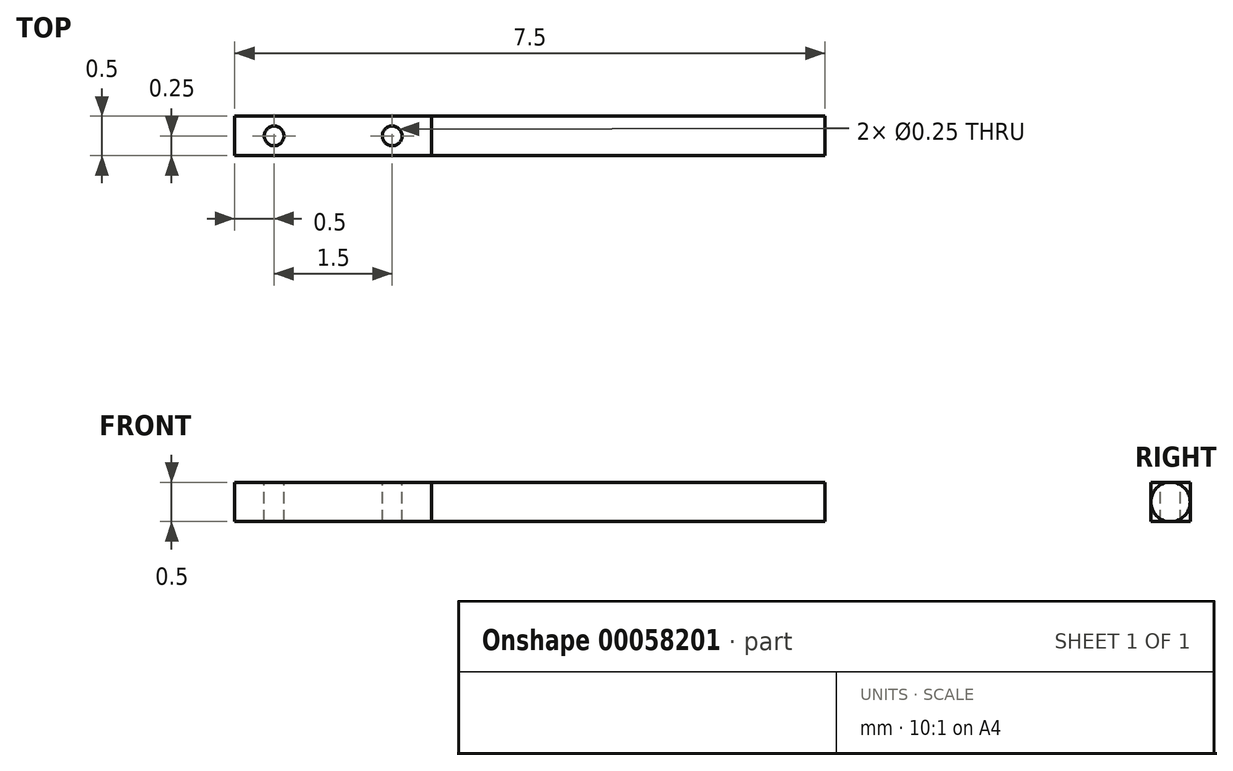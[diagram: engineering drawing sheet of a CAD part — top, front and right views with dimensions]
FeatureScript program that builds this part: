
annotation { "Feature Type Name" : "Feature", "Feature Type Description" : "" }
export const myFeature = defineFeature(function(context is Context, id is Id, definition is map)
    precondition{}
    {
        {
            var Q0;
            Q0=qCreatedBy(makeId("Right.planeOp"),FACE);
            var sketch = newSketch(context, id + "F0", { "sketchPlane" : qUnion([Q0])});
            skLineSegment(sketch, "E0.bottom", {"start": v(-0.25, 0.25) * mm, "end": v(0.25, 0.25) * mm});
            skLineSegment(sketch, "E0.top", {"start": v(-0.25, -0.25) * mm, "end": v(0.25, -0.25) * mm});
            skLineSegment(sketch, "E0.left", {"start": v(-0.25, 0.25) * mm, "end": v(-0.25, -0.25) * mm});
            skLineSegment(sketch, "E0.right", {"start": v(0.25, 0.25) * mm, "end": v(0.25, -0.25) * mm});
            skSolve(sketch);
        }
        {
            var Q0;
            Q0 = qSketchRegion(id + "F0", true);
            extrude(context, id + "F1", {"entities" : qUnion([Q0]), "depth" : 2.5 * mm});
        }
        {
            var Q0;
            Q0=makeQuery(id+"F1.opExtrude","CAP_FACE",FACE,{"disambiguationData":[OSD([sQuery(id+"F0.wireOp",EDGE,"E0.bottom"),sQuery(id+"F0.wireOp",EDGE,"E0.top"),sQuery(id+"F0.wireOp",EDGE,"E0.left"),sQuery(id+"F0.wireOp",EDGE,"E0.right")])],"isStart":false});
            var sketch = newSketch(context, id + "F2", { "sketchPlane" : qUnion([Q0])});
            skCircle(sketch, "E1", {"center": v(0, 0) * mm, "radius": 0.25 * mm});
            skSolve(sketch);
        }
        {
            var Q0;
            Q0 = qSketchRegion(id + "F2", true);
            extrude(context, id + "F3", {"entities" : qUnion([Q0]), "operationType" : NewBodyOperationType.ADD, "depth" : 5 * mm});
        }
        {
            var Q0;
            Q0=makeQuery(id+"F1.opExtrude","SWEPT_FACE",FACE,{"disambiguationData":[OSD([sQuery(id+"F0.wireOp",EDGE,"E0.bottom")])]});
            var sketch = newSketch(context, id + "F4", { "sketchPlane" : qUnion([Q0])});
            skCircle(sketch, "E2", {"center": v(0.5, 0) * mm, "radius": 0.12 * mm});
            skCircle(sketch, "E3", {"center": v(2, 0) * mm, "radius": 0.12 * mm});
            skSolve(sketch);
        }
        {
            var Q0;
            Q0 = qSketchRegion(id + "F4", true);
            extrude(context, id + "F5", {"entities" : qUnion([Q0]), "operationType" : NewBodyOperationType.REMOVE, "oppositeDirection" : true, "depth" : 25 * mm});
        }
    });
